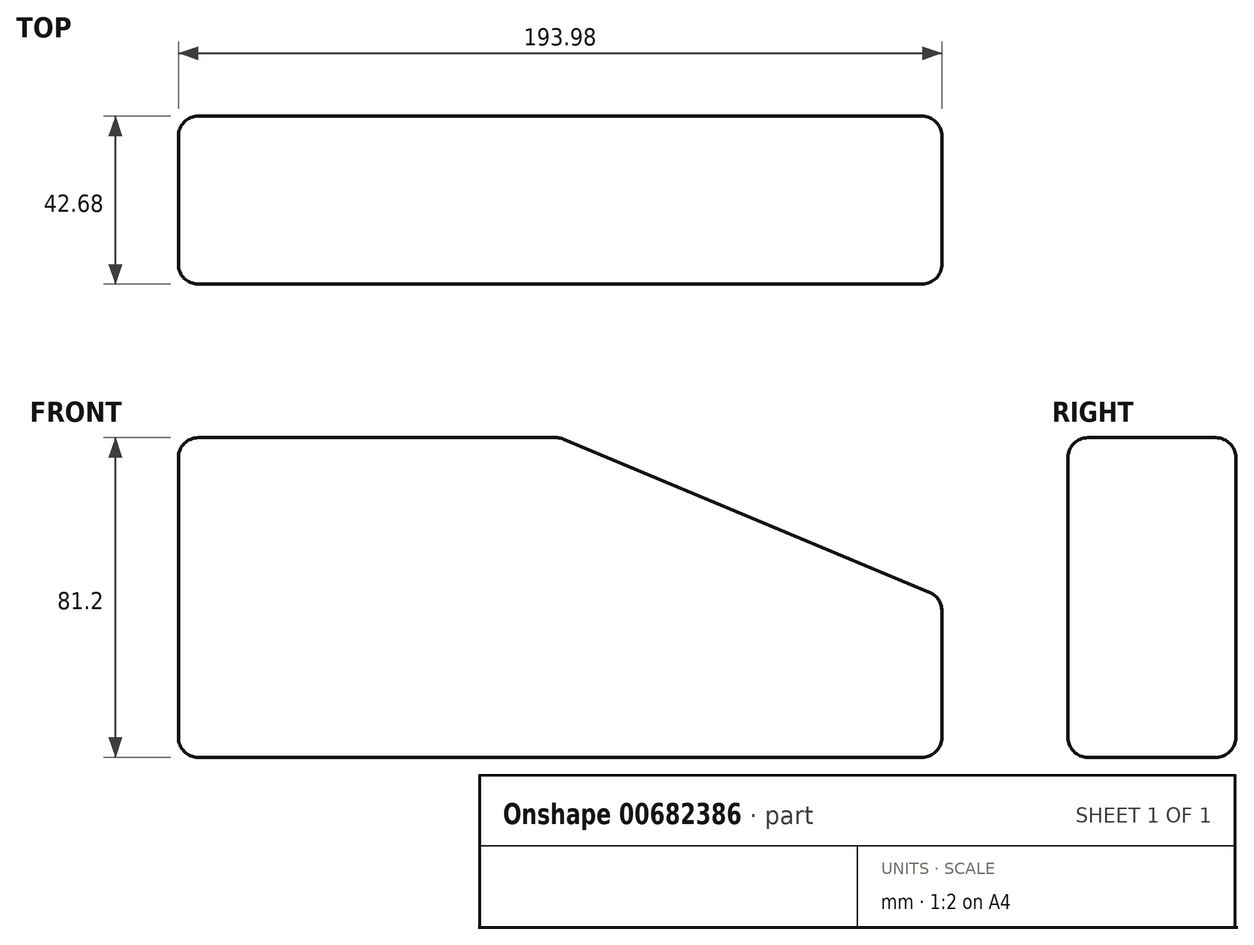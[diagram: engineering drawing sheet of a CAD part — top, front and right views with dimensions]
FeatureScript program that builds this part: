
annotation { "Feature Type Name" : "Feature", "Feature Type Description" : "" }
export const myFeature = defineFeature(function(context is Context, id is Id, definition is map)
    precondition{}
    {
        {
            var Q0;
            Q0=qCreatedBy(makeId("Front.planeOp"),FACE);
            var sketch = newSketch(context, id + "F0", { "sketchPlane" : qUnion([Q0])});
            skLineSegment(sketch, "E0.bottom", {"start": v(-96.99, 40.6) * mm, "end": v(0, 40.6) * mm});
            skLineSegment(sketch, "E0.top", {"start": v(-96.99, -40.6) * mm, "end": v(96.99, -40.6) * mm});
            skLineSegment(sketch, "E0.left", {"start": v(-96.99, 40.6) * mm, "end": v(-96.99, -40.6) * mm});
            skLineSegment(sketch, "E0.right", {"start": v(96.99, 0) * mm, "end": v(96.99, -40.6) * mm});
            skPoint(sketch, "E0.middle", {"position": v(0, 0) * mm});
            skLineSegment(sketch, "E1", {"start": v(96.99, 0) * mm, "end": v(0, 40.6) * mm});
            skPoint(sketch, "E2.orphan", {"position": v(96.99, 40.6) * mm});
            skSolve(sketch);
        }
        {
            var Q0;
            Q0=makeQuery(id+"F0.imprint","IMPRINT",FACE,{"disambiguationData":[TD([[makeQuery(id+"F0.imprint","IMPRINT",EDGE,{"derivedFrom":sQuery(id+"F0.wireOp",EDGE,"E0.bottom")}),-1.0]])]});
            extrude(context, id + "F1", {"entities" : qUnion([Q0]), "endBound" : BoundingType.SYMMETRIC, "depth" : 42.67 * mm, "offsetDistance" : 25.4 * mm});
        }
        {
            var Q0;
            Q0=makeQuery(id+"F1.opExtrude","CAP_EDGE",EDGE,{"disambiguationData":[OSD([sQuery(id+"F0.wireOp",EDGE,"E0.bottom")])],"isStart":false});
            var Q1;
            Q1=makeQuery(id+"F1.opExtrude","CAP_EDGE",EDGE,{"disambiguationData":[OSD([sQuery(id+"F0.wireOp",EDGE,"E1")])],"isStart":false});
            var Q2;
            Q2=makeQuery(id+"F1.opExtrude","CAP_EDGE",EDGE,{"disambiguationData":[OSD([sQuery(id+"F0.wireOp",EDGE,"E0.right")])],"isStart":false});
            var Q3;
            Q3=makeQuery(id+"F1.opExtrude","SWEPT_EDGE",EDGE,{"disambiguationData":[OSD([sQuery(id+"F0.wireOp",EDGE,"E0.right"),sQuery(id+"F0.wireOp",EDGE,"E1")])]});
            var Q4;
            Q4=makeQuery(id+"F1.opExtrude","CAP_EDGE",EDGE,{"disambiguationData":[OSD([sQuery(id+"F0.wireOp",EDGE,"E0.top")])],"isStart":false});
            var Q5;
            Q5=makeQuery(id+"F1.opExtrude","CAP_EDGE",EDGE,{"disambiguationData":[OSD([sQuery(id+"F0.wireOp",EDGE,"E1")])],"isStart":true});
            var Q6;
            Q6=makeQuery(id+"F1.opExtrude","CAP_EDGE",EDGE,{"disambiguationData":[OSD([sQuery(id+"F0.wireOp",EDGE,"E0.bottom")])],"isStart":true});
            var Q7;
            Q7=makeQuery(id+"F1.opExtrude","SWEPT_EDGE",EDGE,{"disambiguationData":[OSD([sQuery(id+"F0.wireOp",EDGE,"E0.bottom"),sQuery(id+"F0.wireOp",EDGE,"E0.left")])]});
            var Q8;
            Q8=makeQuery(id+"F1.opExtrude","CAP_EDGE",EDGE,{"disambiguationData":[OSD([sQuery(id+"F0.wireOp",EDGE,"E0.left")])],"isStart":false});
            var Q9;
            Q9=makeQuery(id+"F1.opExtrude","CAP_EDGE",EDGE,{"disambiguationData":[OSD([sQuery(id+"F0.wireOp",EDGE,"E0.left")])],"isStart":true});
            var Q10;
            Q10=makeQuery(id+"F1.opExtrude","CAP_EDGE",EDGE,{"disambiguationData":[OSD([sQuery(id+"F0.wireOp",EDGE,"E0.top")])],"isStart":true});
            var Q11;
            Q11=makeQuery(id+"F1.opExtrude","SWEPT_EDGE",EDGE,{"disambiguationData":[OSD([sQuery(id+"F0.wireOp",EDGE,"E0.top"),sQuery(id+"F0.wireOp",EDGE,"E0.left")])]});
            var Q12;
            Q12=makeQuery(id+"F1.opExtrude","CAP_EDGE",EDGE,{"disambiguationData":[OSD([sQuery(id+"F0.wireOp",EDGE,"E0.right")])],"isStart":true});
            var Q13;
            Q13=makeQuery(id+"F1.opExtrude","SWEPT_EDGE",EDGE,{"disambiguationData":[OSD([sQuery(id+"F0.wireOp",EDGE,"E0.top"),sQuery(id+"F0.wireOp",EDGE,"E0.right")])]});
            var Q14;
            Q14=makeQuery(id+"F1.opExtrude","SWEPT_EDGE",EDGE,{"disambiguationData":[OSD([sQuery(id+"F0.wireOp",EDGE,"E0.bottom"),sQuery(id+"F0.wireOp",EDGE,"E1")])]});
            fillet(context, id + "F2", {"entities" : qUnion([Q0, Q1, Q2, Q3, Q4, Q5, Q6, Q7, Q8, Q9, Q10, Q11, Q12, Q13, Q14]), "radius" : 5.08 * mm, "tangentPropagation" : true, "allowEdgeOverflow" : false});
        }
    });
